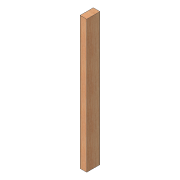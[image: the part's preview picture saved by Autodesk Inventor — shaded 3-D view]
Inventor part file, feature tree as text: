
AUTODESK INVENTOR PART (.ipt)
format: ipt  version: 2016 (Build 200138000, 138)  size: 95,744 bytes
history: native  units: in
note: dims shown in document units (in); Inventor stores cm internally (conversion verified against a paired STEP export)
features: extrude x1, sketch x1
ambient origin geometry x8: Origin, YZ Plane, XZ Plane, XY Plane, X Axis, Y Axis, Z Axis, Center Point
bodies: Solid1 (feature_tree)
feature tree (2):
  extrude  "Extrusion1"  Depth=4.0in
  sketch  "Sketch1"  dims[d0=2.0in d1=4.0in d2=40.0in d3=0.0in]
